# Revit family: PH_2915-2965-2606_OS275
name_source: partatom
category: Finestre
units: mm (PartAtom-declared; Revit-internal decimal feet)

## family parameters
Condiviso = No
Host = Muro
Numero OmniClass = 23.30.20.00
Punto di calcolo locali = Sì
Sempre verticale = Sì
Taglio con vuoti quando caricato = No
Titolo OmniClass = Windows

## types (4) — shared parameters
Altezza di default del davanzale = 800 mm  [stored 2.62467 ft]
Altezza_1A = 635 mm
Altezza_2A = 635 mm
Altezza_ante = 1270 mm
Chiusura muro = Per host
Costruzione analitica = <Nessuno>
Descrizione = finestra a bilico orizzontale
H1 = 1300 mm
H_Max = 1300 mm
H_Min = 600 mm
H_Telaio_E = 650 mm  [stored 2.13255 ft]
H_Telaio_I = 650 mm  [stored 2.13255 ft]
H_vetro = 1194 mm
L_Max = 2000 mm  [stored 6.56168 ft]
L_Min = 600 mm
Modello = OS2 75
Produttore = Secco Sistemi Spa
URL = https://www.seccosistemi.com
WARNING = Sì

## per-type parameters (varying)
| type | Altezza | L1 | L_Telaio_E | L_Telaio_I | L_vetro | Larghezza | Larghezza_ante | MATERIALE |
| Ottone | 2000 mm  [stored 6.56168 ft] | 2000 mm  [stored 6.56168 ft] | 1000 mm  [stored 3.28084 ft] | 1000 mm  [stored 3.28084 ft] | 1894 mm  [stored 6.21391 ft] | 2000 mm  [stored 6.56168 ft] | 1970 mm  [stored 6.46325 ft] | Ottone |
| Acciaio zincato | 1500 mm | 1000 mm  [stored 3.28084 ft] | 500 mm  [stored 1.64042 ft] | 500 mm  [stored 1.64042 ft] | 894 mm | 1000 mm  [stored 3.28084 ft] | 970 mm  [stored 3.18241 ft] | Acciaio |
| Acciaio inox | 1500 mm | 1000 mm  [stored 3.28084 ft] | 500 mm  [stored 1.64042 ft] | 500 mm  [stored 1.64042 ft] | 894 mm | 1000 mm  [stored 3.28084 ft] | 970 mm  [stored 3.18241 ft] | Acciaio inox, spazzolato |
| Acciaio Corten | 1500 mm | 1000 mm  [stored 3.28084 ft] | 500 mm  [stored 1.64042 ft] | 500 mm  [stored 1.64042 ft] | 894 mm | 1000 mm  [stored 3.28084 ft] | 970 mm  [stored 3.18241 ft] | Acciaio corten |

note: [stored X ft] marks values corroborated as IEEE doubles in the binary element streams (Revit-internal decimal feet)
